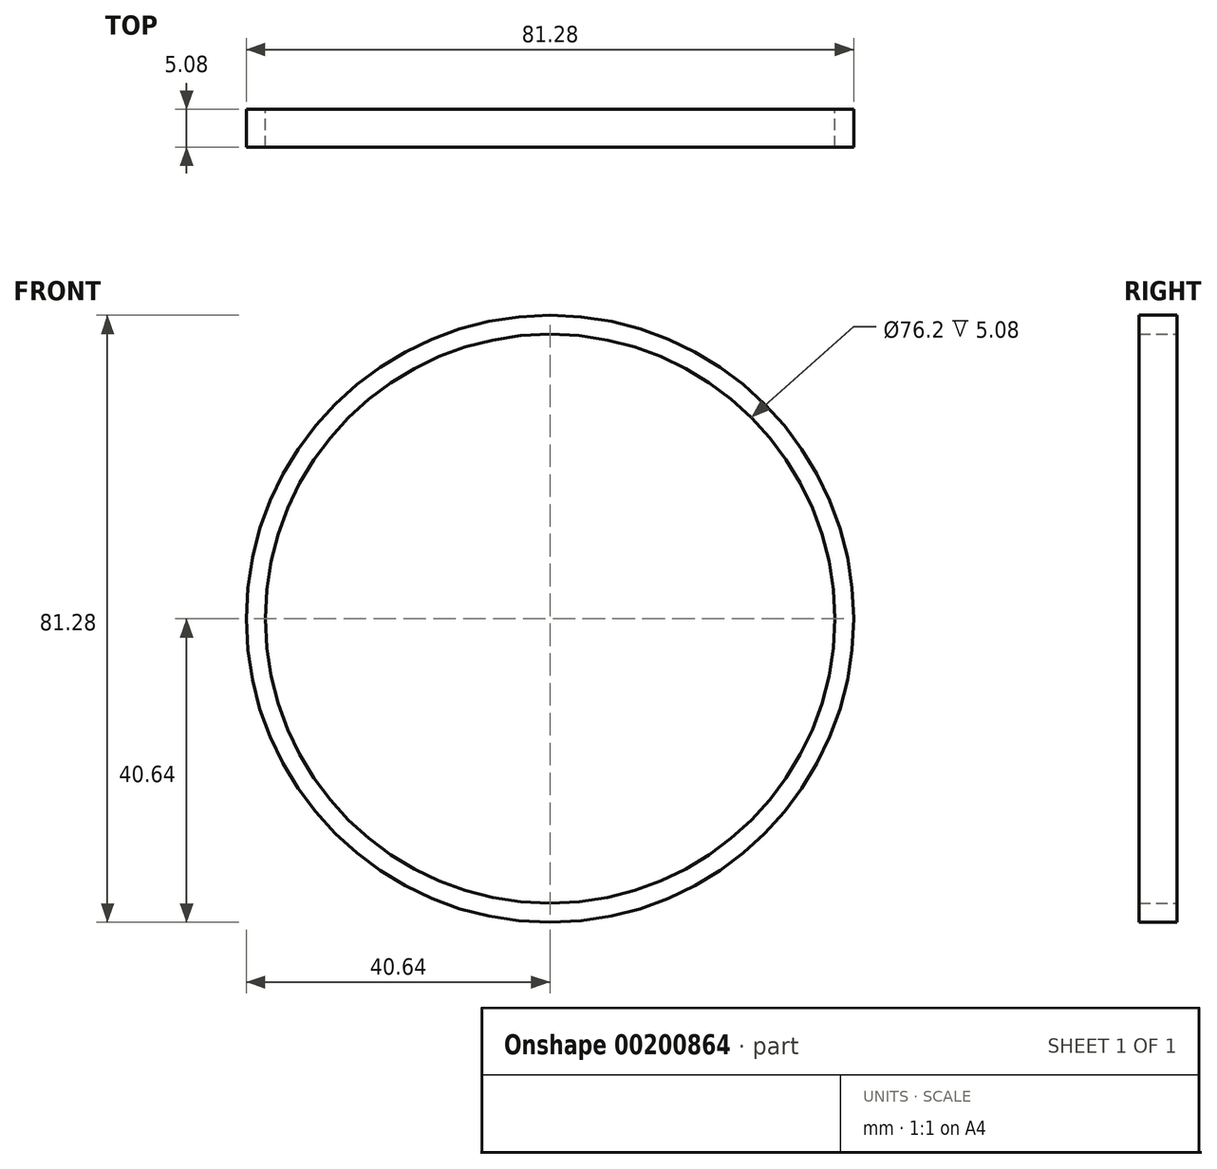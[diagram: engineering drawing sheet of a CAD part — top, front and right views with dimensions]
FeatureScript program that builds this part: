
annotation { "Feature Type Name" : "Feature", "Feature Type Description" : "" }
export const myFeature = defineFeature(function(context is Context, id is Id, definition is map)
    precondition{}
    {
        {
            var Q0;
            Q0=qCreatedBy(makeId("Front.planeOp"),FACE);
            var sketch = newSketch(context, id + "F0", { "sketchPlane" : qUnion([Q0])});
            skCircle(sketch, "E0", {"center": v(0, 0) * mm, "radius": 40.64 * mm});
            skCircle(sketch, "E1", {"center": v(0, 0) * mm, "radius": 38.1 * mm});
            skLineSegment(sketch, "E2", {"start": v(0, 38.1) * mm, "end": v(0, 40.64) * mm});
            skSolve(sketch);
        }
        {
            var Q0;
            Q0 = qSketchRegion(id + "F0", true);
            extrude(context, id + "F1", {"entities" : qUnion([Q0]), "depth" : 5.08 * mm});
        }
    });
